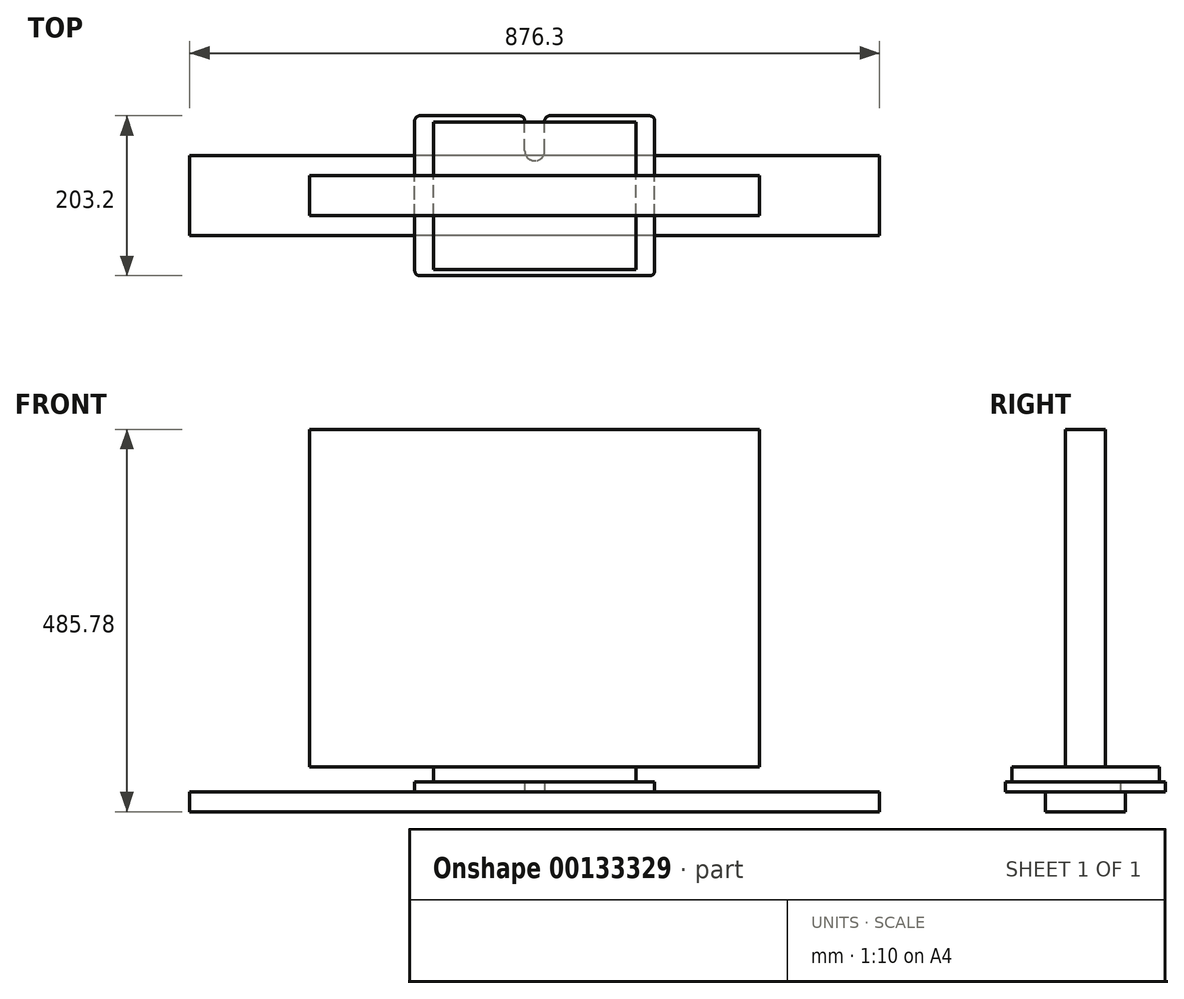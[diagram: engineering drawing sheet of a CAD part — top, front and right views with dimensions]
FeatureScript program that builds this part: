
annotation { "Feature Type Name" : "Feature", "Feature Type Description" : "" }
export const myFeature = defineFeature(function(context is Context, id is Id, definition is map)
    precondition{}
    {
        {
            var Q0;
            Q0=qCreatedBy(makeId("Top.planeOp"),FACE);
            var sketch = newSketch(context, id + "F0", { "sketchPlane" : qUnion([Q0])});
            skLineSegment(sketch, "E0.bottom", {"start": v(146.05, -101.6) * mm, "end": v(-146.05, -101.6) * mm});
            skLineSegment(sketch, "E0.top", {"start": v(146.05, 101.6) * mm, "end": v(19.05, 101.6) * mm});
            skLineSegment(sketch, "E0.left", {"start": v(152.4, -95.25) * mm, "end": v(152.4, 95.25) * mm});
            skLineSegment(sketch, "E0.right", {"start": v(-152.4, -95.25) * mm, "end": v(-152.4, 95.25) * mm});
            skPoint(sketch, "E0.middle", {"position": v(0, 0) * mm});
            skLineSegment(sketch, "E1", {"start": v(0, 0) * mm, "end": v(0, 144.7) * mm, "construction": true});
            skPoint(sketch, "E1.endSnap0", {"position": v(0, 101.6) * mm});
            skArc(sketch, "E2", {"start": v(-12.7, 57.15) * mm, "mid": v(0, 44.45) * mm, "end": v(12.7, 57.15) * mm});
            skLineSegment(sketch, "E3", {"start": v(24.67, 57.15) * mm, "end": v(-20.13, 57.15) * mm, "construction": true});
            skLineSegment(sketch, "E4", {"start": v(-12.7, 57.15) * mm, "end": v(-12.7, 95.25) * mm});
            skLineSegment(sketch, "E5.MirrorCS", {"start": v(12.7, 57.15) * mm, "end": v(12.7, 95.25) * mm});
            skLineSegment(sketch, "E6.trimOffspring", {"start": v(-19.05, 101.6) * mm, "end": v(-146.05, 101.6) * mm});
            skPoint(sketch, "E7.visualSharp", {"position": v(-152.4, 101.6) * mm});
            skArc(sketch, "E7.filletArc", {"start": v(-146.05, 101.6) * mm, "mid": v(-150.54, 99.74) * mm, "end": v(-152.4, 95.25) * mm});
            skPoint(sketch, "E8.visualSharp", {"position": v(152.4, 101.6) * mm});
            skArc(sketch, "E8.filletArc", {"start": v(152.4, 95.25) * mm, "mid": v(150.54, 99.74) * mm, "end": v(146.05, 101.6) * mm});
            skPoint(sketch, "E9.visualSharp", {"position": v(152.4, -101.6) * mm});
            skArc(sketch, "E9.filletArc", {"start": v(146.05, -101.6) * mm, "mid": v(150.54, -99.74) * mm, "end": v(152.4, -95.25) * mm});
            skPoint(sketch, "E10.visualSharp", {"position": v(-152.4, -101.6) * mm});
            skArc(sketch, "E10.filletArc", {"start": v(-152.4, -95.25) * mm, "mid": v(-150.54, -99.74) * mm, "end": v(-146.05, -101.6) * mm});
            skPoint(sketch, "E11.visualSharp", {"position": v(-12.7, 101.6) * mm});
            skArc(sketch, "E11.filletArc", {"start": v(-12.7, 95.25) * mm, "mid": v(-14.56, 99.74) * mm, "end": v(-19.05, 101.6) * mm});
            skPoint(sketch, "E12.visualSharp", {"position": v(12.7, 101.6) * mm});
            skArc(sketch, "E12.filletArc", {"start": v(19.05, 101.6) * mm, "mid": v(14.56, 99.74) * mm, "end": v(12.7, 95.25) * mm});
            skSolve(sketch);
        }
        {
            var Q0;
            Q0=makeQuery(id+"F0.imprint","IMPRINT",FACE,{"disambiguationData":[TD([[makeQuery(id+"F0.imprint","IMPRINT",EDGE,{"derivedFrom":sQuery(id+"F0.wireOp",EDGE,"E0.bottom")}),-1.0]])]});
            extrude(context, id + "F1", {"entities" : qUnion([Q0]), "depth" : 12.7 * mm});
        }
        {
            var Q0;
            Q0=makeQuery(id+"F1.opExtrude","CAP_FACE",FACE,{"disambiguationData":[OSD([sQuery(id+"F0.wireOp",EDGE,"E0.bottom"),sQuery(id+"F0.wireOp",EDGE,"E0.top"),sQuery(id+"F0.wireOp",EDGE,"E0.left"),sQuery(id+"F0.wireOp",EDGE,"E0.right"),sQuery(id+"F0.wireOp",EDGE,"E2"),sQuery(id+"F0.wireOp",EDGE,"E4"),sQuery(id+"F0.wireOp",EDGE,"E5.MirrorCS"),sQuery(id+"F0.wireOp",EDGE,"E6.trimOffspring"),sQuery(id+"F0.wireOp",EDGE,"E7.filletArc"),sQuery(id+"F0.wireOp",EDGE,"E8.filletArc"),sQuery(id+"F0.wireOp",EDGE,"E9.filletArc"),sQuery(id+"F0.wireOp",EDGE,"E10.filletArc"),sQuery(id+"F0.wireOp",EDGE,"E11.filletArc"),sQuery(id+"F0.wireOp",EDGE,"E12.filletArc")])],"isStart":true});
            var sketch = newSketch(context, id + "F2", { "sketchPlane" : qUnion([Q0])});
            skLineSegment(sketch, "E13.bottom", {"start": v(438.15, -50.8) * mm, "end": v(-438.15, -50.8) * mm});
            skLineSegment(sketch, "E13.top", {"start": v(438.15, 50.8) * mm, "end": v(-438.15, 50.8) * mm});
            skLineSegment(sketch, "E13.left", {"start": v(438.15, -50.8) * mm, "end": v(438.15, 50.8) * mm});
            skLineSegment(sketch, "E13.right", {"start": v(-438.15, -50.8) * mm, "end": v(-438.15, 50.8) * mm});
            skPoint(sketch, "E13.middle", {"position": v(0, 0) * mm});
            skSolve(sketch);
        }
        {
            var Q0;
            Q0 = qSketchRegion(id + "F2", true);
            extrude(context, id + "F3", {"entities" : qUnion([Q0]), "operationType" : NewBodyOperationType.ADD, "depth" : 25.4 * mm});
        }
        {
            var Q0;
            Q0=makeQuery(id+"F1.opExtrude","CAP_FACE",FACE,{"disambiguationData":[OSD([sQuery(id+"F0.wireOp",EDGE,"E0.bottom"),sQuery(id+"F0.wireOp",EDGE,"E0.top"),sQuery(id+"F0.wireOp",EDGE,"E0.left"),sQuery(id+"F0.wireOp",EDGE,"E0.right"),sQuery(id+"F0.wireOp",EDGE,"E2"),sQuery(id+"F0.wireOp",EDGE,"E4"),sQuery(id+"F0.wireOp",EDGE,"E5.MirrorCS"),sQuery(id+"F0.wireOp",EDGE,"E6.trimOffspring"),sQuery(id+"F0.wireOp",EDGE,"E7.filletArc"),sQuery(id+"F0.wireOp",EDGE,"E8.filletArc"),sQuery(id+"F0.wireOp",EDGE,"E9.filletArc"),sQuery(id+"F0.wireOp",EDGE,"E10.filletArc"),sQuery(id+"F0.wireOp",EDGE,"E11.filletArc"),sQuery(id+"F0.wireOp",EDGE,"E12.filletArc")])],"isStart":false});
            var sketch = newSketch(context, id + "F4", { "sketchPlane" : qUnion([Q0])});
            skLineSegment(sketch, "E14.bottom", {"start": v(128.59, -93.66) * mm, "end": v(-128.59, -93.66) * mm});
            skLineSegment(sketch, "E14.top", {"start": v(128.59, 93.66) * mm, "end": v(-128.59, 93.66) * mm});
            skLineSegment(sketch, "E14.left", {"start": v(128.59, -93.66) * mm, "end": v(128.59, 93.66) * mm});
            skLineSegment(sketch, "E14.right", {"start": v(-128.59, -93.66) * mm, "end": v(-128.59, 93.66) * mm});
            skPoint(sketch, "E14.middle", {"position": v(0, 0) * mm});
            skSolve(sketch);
        }
        {
            var Q0;
            Q0 = qSketchRegion(id + "F4", true);
            extrude(context, id + "F5", {"entities" : qUnion([Q0]), "operationType" : NewBodyOperationType.ADD, "depth" : 19.05 * mm});
        }
        {
            var Q0;
            Q0=makeQuery(id+"F5.opExtrude","CAP_FACE",FACE,{"disambiguationData":[OSD([sQuery(id+"F4.wireOp",EDGE,"E14.bottom"),sQuery(id+"F4.wireOp",EDGE,"E14.top"),sQuery(id+"F4.wireOp",EDGE,"E14.left"),sQuery(id+"F4.wireOp",EDGE,"E14.right")])],"isStart":false});
            var sketch = newSketch(context, id + "F6", { "sketchPlane" : qUnion([Q0])});
            skLineSegment(sketch, "E15.bottom", {"start": v(285.75, -25.4) * mm, "end": v(-285.75, -25.4) * mm});
            skLineSegment(sketch, "E15.top", {"start": v(285.75, 25.4) * mm, "end": v(-285.75, 25.4) * mm});
            skLineSegment(sketch, "E15.left", {"start": v(285.75, -25.4) * mm, "end": v(285.75, 25.4) * mm});
            skLineSegment(sketch, "E15.right", {"start": v(-285.75, -25.4) * mm, "end": v(-285.75, 25.4) * mm});
            skPoint(sketch, "E15.middle", {"position": v(0, 0) * mm});
            skSolve(sketch);
        }
        {
            var Q0;
            Q0 = qSketchRegion(id + "F6", true);
            extrude(context, id + "F7", {"entities" : qUnion([Q0]), "operationType" : NewBodyOperationType.ADD, "depth" : 428.62 * mm});
        }
    });
